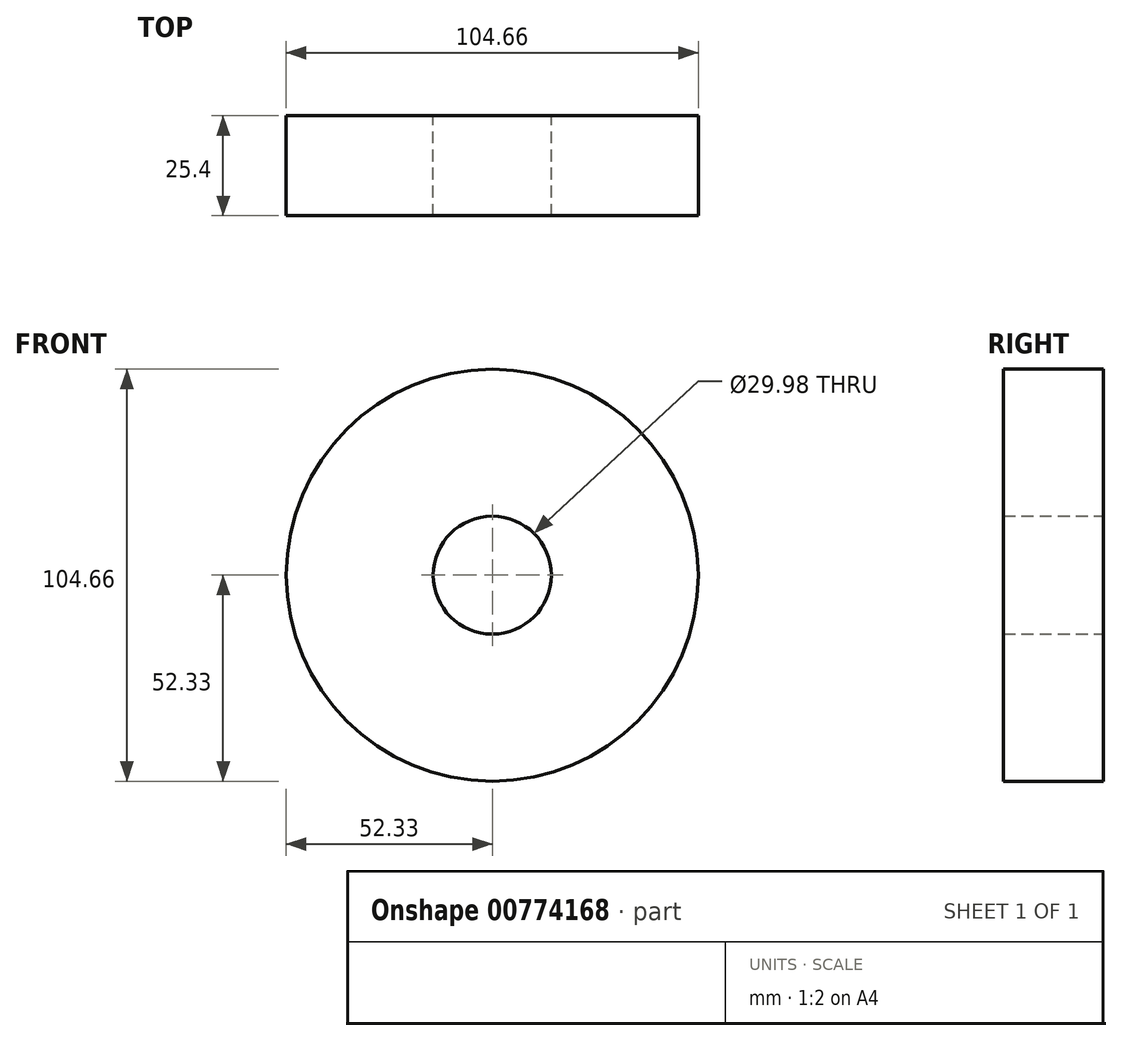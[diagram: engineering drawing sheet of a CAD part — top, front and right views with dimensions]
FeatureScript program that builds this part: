
annotation { "Feature Type Name" : "Feature", "Feature Type Description" : "" }
export const myFeature = defineFeature(function(context is Context, id is Id, definition is map)
    precondition{}
    {
        {
            var Q0;
            Q0=qCreatedBy(makeId("Front.planeOp"),FACE);
            var sketch = newSketch(context, id + "F0", { "sketchPlane" : qUnion([Q0])});
            skCircle(sketch, "E0", {"center": v(0, 0) * mm, "radius": 14.99 * mm});
            skCircle(sketch, "E1", {"center": v(0, 0) * mm, "radius": 52.33 * mm});
            skSolve(sketch);
        }
        {
            var Q0;
            Q0=makeQuery(id+"F0.imprint","IMPRINT",FACE,{"disambiguationData":[TD([[makeQuery(id+"F0.imprint","IMPRINT",EDGE,{"derivedFrom":sQuery(id+"F0.wireOp",EDGE,"E0")}),-1.0]])]});
            extrude(context, id + "F1", {"entities" : qUnion([Q0]), "depth" : 25.4 * mm, "offsetDistance" : 25.4 * mm});
        }
    });
